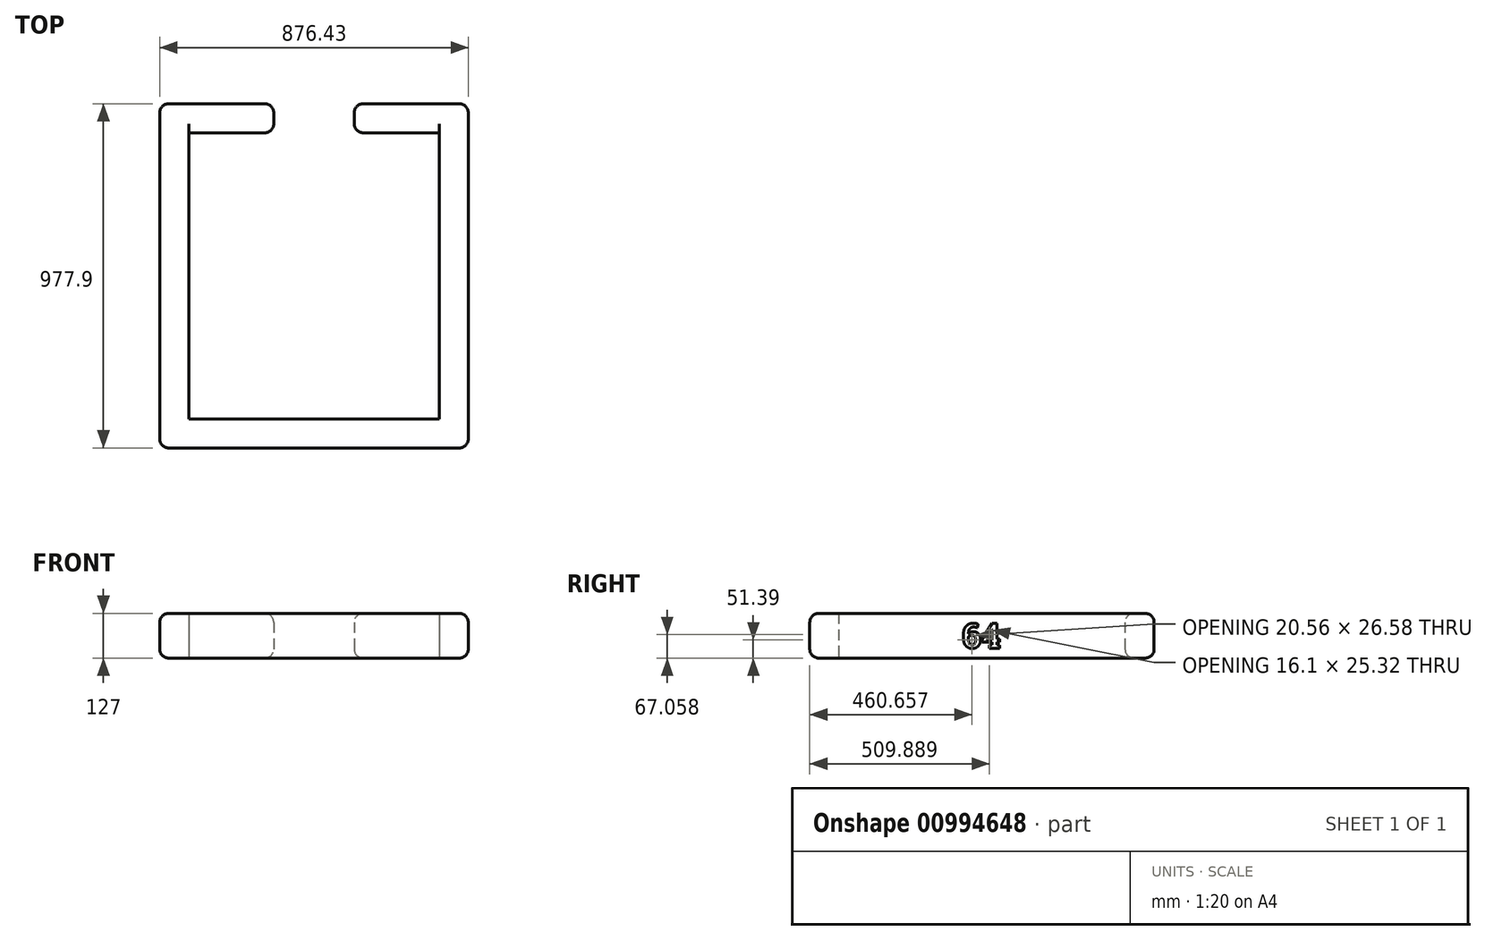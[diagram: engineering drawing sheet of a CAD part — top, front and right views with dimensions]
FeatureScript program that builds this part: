
annotation { "Feature Type Name" : "Feature", "Feature Type Description" : "" }
export const myFeature = defineFeature(function(context is Context, id is Id, definition is map)
    precondition{}
    {
        {
            var Q0;
            Q0=qCreatedBy(makeId("Top.planeOp"),FACE);
            var sketch = newSketch(context, id + "F0", { "sketchPlane" : qUnion([Q0])});
            skLineSegment(sketch, "E0.top", {"start": v(330.2, -406.4) * mm, "end": v(-330.2, -406.4) * mm});
            skLineSegment(sketch, "E0.left", {"start": v(355.6, 381) * mm, "end": v(355.6, -381) * mm});
            skLineSegment(sketch, "E0.right", {"start": v(-355.6, 381) * mm, "end": v(-355.6, -381) * mm});
            skPoint(sketch, "E0.middle", {"position": v(0, 0) * mm});
            skLineSegment(sketch, "E1", {"start": v(-330.2, 406.4) * mm, "end": v(-139.7, 406.4) * mm});
            skLineSegment(sketch, "E2", {"start": v(330.2, 406.4) * mm, "end": v(139.7, 406.4) * mm});
            skLineSegment(sketch, "E3", {"start": v(114.3, 431.8) * mm, "end": v(114.3, 463.55) * mm});
            skLineSegment(sketch, "E4", {"start": v(139.7, 488.95) * mm, "end": v(412.75, 488.95) * mm});
            skLineSegment(sketch, "E5", {"start": v(438.15, 463.55) * mm, "end": v(438.15, -463.55) * mm});
            skLineSegment(sketch, "E6", {"start": v(412.75, -488.95) * mm, "end": v(-412.75, -488.95) * mm});
            skLineSegment(sketch, "E7", {"start": v(-438.15, -463.55) * mm, "end": v(-438.15, 463.55) * mm});
            skLineSegment(sketch, "E8", {"start": v(-412.75, 488.95) * mm, "end": v(-139.7, 488.95) * mm});
            skLineSegment(sketch, "E9", {"start": v(-114.3, 431.8) * mm, "end": v(-114.3, 463.55) * mm});
            skPoint(sketch, "E10.visualSharp", {"position": v(-438.15, 488.95) * mm});
            skArc(sketch, "E10.filletArc", {"start": v(-412.75, 488.95) * mm, "mid": v(-430.71, 481.51) * mm, "end": v(-438.15, 463.55) * mm});
            skPoint(sketch, "E11.visualSharp", {"position": v(-114.3, 488.95) * mm});
            skArc(sketch, "E11.filletArc", {"start": v(-114.3, 463.55) * mm, "mid": v(-121.74, 481.51) * mm, "end": v(-139.7, 488.95) * mm});
            skPoint(sketch, "E12.visualSharp", {"position": v(-114.3, 406.4) * mm});
            skArc(sketch, "E12.filletArc", {"start": v(-139.7, 406.4) * mm, "mid": v(-121.74, 413.84) * mm, "end": v(-114.3, 431.8) * mm});
            skPoint(sketch, "E13.visualSharp", {"position": v(114.3, 488.95) * mm});
            skArc(sketch, "E13.filletArc", {"start": v(139.7, 488.95) * mm, "mid": v(121.74, 481.51) * mm, "end": v(114.3, 463.55) * mm});
            skPoint(sketch, "E14.visualSharp", {"position": v(114.3, 406.4) * mm});
            skArc(sketch, "E14.filletArc", {"start": v(114.3, 431.8) * mm, "mid": v(121.74, 413.84) * mm, "end": v(139.7, 406.4) * mm});
            skPoint(sketch, "E15.visualSharp", {"position": v(438.15, 488.95) * mm});
            skArc(sketch, "E15.filletArc", {"start": v(438.15, 463.55) * mm, "mid": v(430.71, 481.51) * mm, "end": v(412.75, 488.95) * mm});
            skPoint(sketch, "E16.visualSharp", {"position": v(355.6, 406.4) * mm});
            skArc(sketch, "E16.filletArc", {"start": v(355.6, 381) * mm, "mid": v(355.58, 382.13) * mm, "end": v(355.5, 383.25) * mm});
            skPoint(sketch, "E17.visualSharp", {"position": v(355.6, -406.4) * mm});
            skPoint(sketch, "E18.visualSharp", {"position": v(438.15, -488.95) * mm});
            skArc(sketch, "E18.filletArc", {"start": v(412.75, -488.95) * mm, "mid": v(430.71, -481.51) * mm, "end": v(438.15, -463.55) * mm});
            skPoint(sketch, "E19.visualSharp", {"position": v(-438.15, -488.95) * mm});
            skArc(sketch, "E19.filletArc", {"start": v(-438.15, -463.55) * mm, "mid": v(-430.71, -481.51) * mm, "end": v(-412.75, -488.95) * mm});
            skPoint(sketch, "E20.visualSharp", {"position": v(-355.6, -406.4) * mm});
            skPoint(sketch, "E21.visualSharp", {"position": v(-355.6, 406.4) * mm});
            skLineSegment(sketch, "E22", {"start": v(330.2, 406.4) * mm, "end": v(355.6, 406.4) * mm});
            skLineSegment(sketch, "E23", {"start": v(355.6, 406.4) * mm, "end": v(355.6, 381) * mm});
            skLineSegment(sketch, "E24", {"start": v(355.6, -406.4) * mm, "end": v(355.6, -381) * mm});
            skLineSegment(sketch, "E25", {"start": v(355.6, -406.4) * mm, "end": v(330.2, -406.4) * mm});
            skLineSegment(sketch, "E26", {"start": v(-330.2, -406.4) * mm, "end": v(-355.6, -406.4) * mm});
            skLineSegment(sketch, "E27", {"start": v(-355.6, -381) * mm, "end": v(-355.6, -406.4) * mm});
            skLineSegment(sketch, "E28", {"start": v(-355.6, 381) * mm, "end": v(-355.6, 406.4) * mm});
            skLineSegment(sketch, "E29", {"start": v(-355.6, 406.4) * mm, "end": v(-330.2, 406.4) * mm});
            skSolve(sketch);
        }
        {
            var Q0;
            Q0 = qSketchRegion(id + "F0", true);
            extrude(context, id + "F1", {"entities" : qUnion([Q0]), "depth" : 127 * mm, "offsetDistance" : 25.4 * mm});
        }
        {
            var Q0;
            Q0=makeQuery(id+"F1.opExtrude","SWEPT_FACE",FACE,{"disambiguationData":[OSD([sQuery(id+"F0.wireOp",EDGE,"E5")])]});
            var sketch = newSketch(context, id + "F2", { "sketchPlane" : qUnion([Q0])});
            skLineSegment(sketch, "E30", {"start": v(-463.55, 127) * mm, "end": v(463.55, 127) * mm, "construction": true});
            skPoint(sketch, "E31", {"position": v(0, 127) * mm});
            skLineSegment(sketch, "E32", {"start": v(-463.55, 63.5) * mm, "end": v(463.55, 63.5) * mm, "construction": true});
            skText(sketch, "E33", { "text": "64\n", "fontName": "RobotoSlab-Bold.ttf"});
            skLineSegment(sketch, "E34", {"start": v(0, 127) * mm, "end": v(0, 0) * mm, "construction": true});
            const initialGuessF2  = {"E33": [-0.05693, 0.02835, 1, 0, 0.07085]};
            skSetInitialGuess(sketch, initialGuessF2);
            skSolve(sketch);
        }
        {
            var Q0;
            Q0 = qSketchRegion(id + "F2", true);
            var Q1;
            Q1=sQuery(id+"F2.wireOp",EDGE,"c8NivUqi-Z9Z3-N2P9-6HmX-gAWwql7rXYCS");
            var Q2;
            Q2=sQuery(id+"F2.wireOp",EDGE,"LYhiiuMp-GgvA-pv6E-rN37-O8gmNIkAs5Sf");
            extrude(context, id + "F3", {"entities" : qUnion([Q0]), "surfaceEntities" : qUnion([Q1, Q2]), "depth" : 0.13 * mm, "offsetDistance" : 25.4 * mm});
        }
        {
            var Q0;
            Q0=makeQuery(id+"F1.opExtrude","CAP_EDGE",EDGE,{"disambiguationData":[OSD([sQuery(id+"F0.wireOp",EDGE,"E5")])],"isStart":false});
            fillet(context, id + "F4", {"entities" : qUnion([Q0]), "radius" : 25.4 * mm, "tangentPropagation" : true, "allowEdgeOverflow" : false});
        }
        {
            var Q0;
            Q0=makeQuery(id+"F1.opExtrude","CAP_EDGE",EDGE,{"disambiguationData":[OSD([sQuery(id+"F0.wireOp",EDGE,"E6")])],"isStart":true});
            fillet(context, id + "F5", {"entities" : qUnion([Q0]), "radius" : 25.4 * mm, "tangentPropagation" : true, "allowEdgeOverflow" : false});
        }
    });
